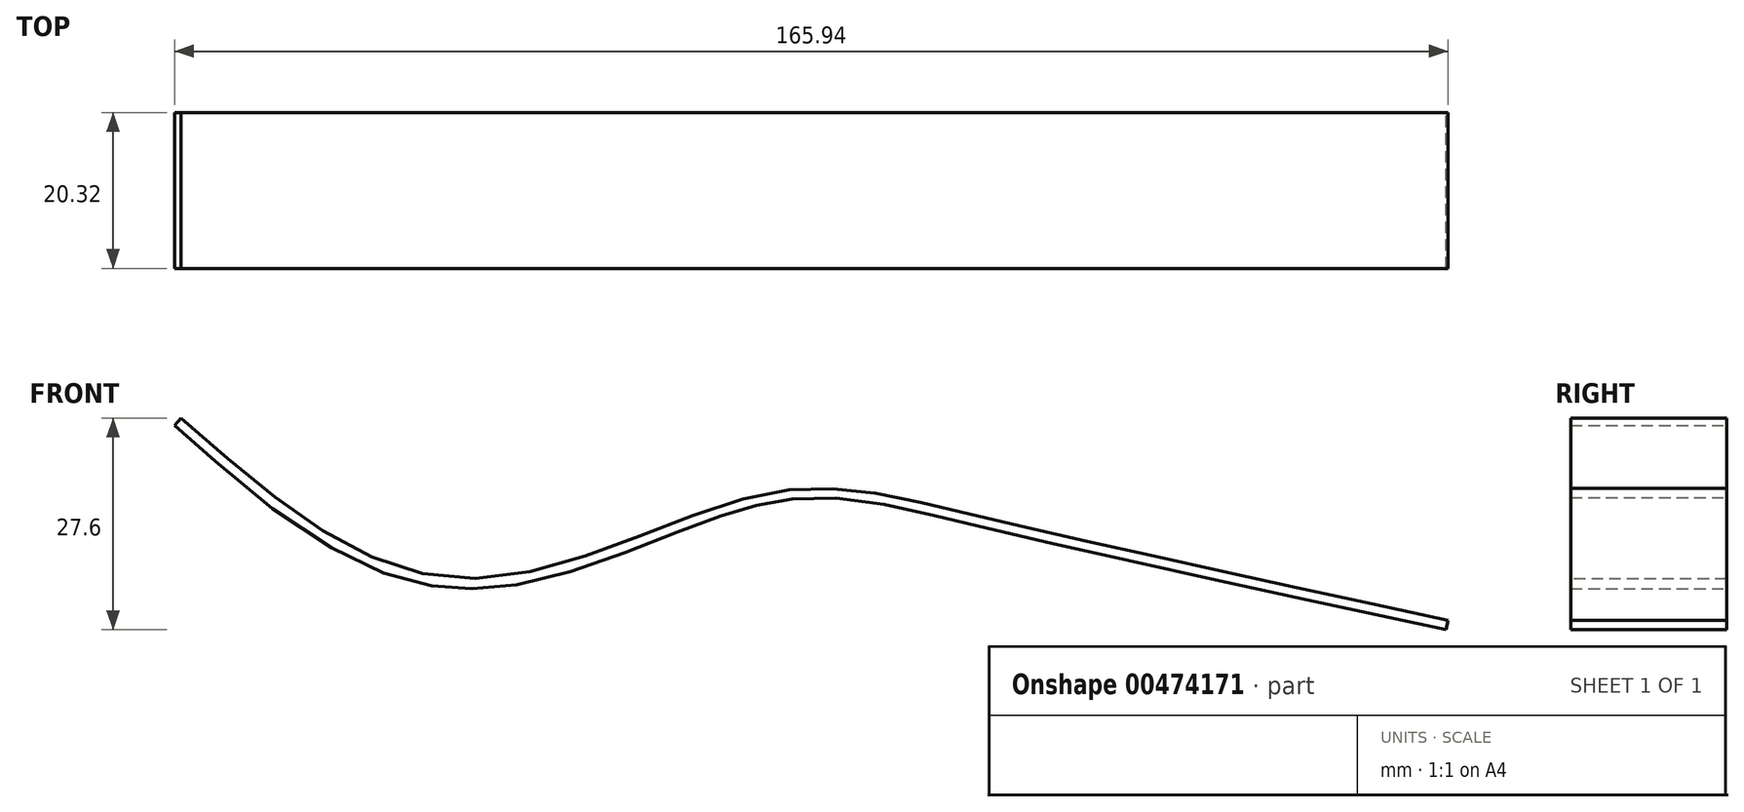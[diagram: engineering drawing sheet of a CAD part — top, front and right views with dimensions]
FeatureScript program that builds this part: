
annotation { "Feature Type Name" : "Feature", "Feature Type Description" : "" }
export const myFeature = defineFeature(function(context is Context, id is Id, definition is map)
    precondition{}
    {
        {
            var Q0;
            Q0=qCreatedBy(makeId("Front.planeOp"),FACE);
            var sketch = newSketch(context, id + "F0", { "sketchPlane" : qUnion([Q0])});
            skFitSpline(sketch, "E0", {"points": [v(0, 0) * mm, v(36.43, -20.93) * mm, v(75.19, -10.08) * mm, v(102.32, -12.4) * mm, v(165.1, -26.35) * mm], "startDerivative": vector(140.12, -123.04) * mm, "endDerivative": vector(227.92, -49.3) * mm});
            skFitSpline(sketch, "E1.0", {"points": [v(-0.84, -0.95) * mm, v(2.08, -3.52) * mm, v(7.94, -8.66) * mm, v(15.45, -14.38) * mm, v(21.68, -18.05) * mm, v(26.48, -20.23) * mm, v(30.61, -21.47) * mm, v(34, -22.04) * mm, v(36.6, -22.24) * mm, v(39.21, -22.21) * mm, v(42.72, -21.88) * mm, v(47.13, -21.02) * mm, v(52.4, -19.47) * mm, v(57.6, -17.6) * mm, v(62.68, -15.63) * mm, v(66.77, -14.05) * mm, v(69.92, -12.93) * mm, v(72.21, -12.18) * mm, v(74.43, -11.55) * mm, v(76.55, -11.06) * mm, v(78.6, -10.72) * mm, v(81.26, -10.43) * mm, v(84.5, -10.38) * mm, v(88.37, -10.72) * mm, v(92.37, -11.4) * mm, v(96.6, -12.33) * mm, v(101.2, -13.44) * mm, v(106.25, -14.64) * mm, v(113.54, -16.33) * mm, v(123.57, -18.6) * mm, v(136.7, -21.5) * mm, v(150.59, -24.51) * mm, v(160.08, -26.57) * mm, v(164.83, -27.6) * mm]});
            skLineSegment(sketch, "E2", {"start": v(-0.84, -0.95) * mm, "end": v(0, 0) * mm});
            skLineSegment(sketch, "E3", {"start": v(164.83, -27.6) * mm, "end": v(165.1, -26.35) * mm});
            skSolve(sketch);
        }
        {
            var Q0;
            Q0=makeQuery(id+"F0.imprint","IMPRINT",FACE,{"disambiguationData":[TD([[makeQuery(id+"F0.imprint","IMPRINT",EDGE,{"derivedFrom":sQuery(id+"F0.wireOp",EDGE,"E0")}),-1.0]])]});
            extrude(context, id + "F1", {"entities" : qUnion([Q0]), "depth" : 20.32 * mm});
        }
    });
